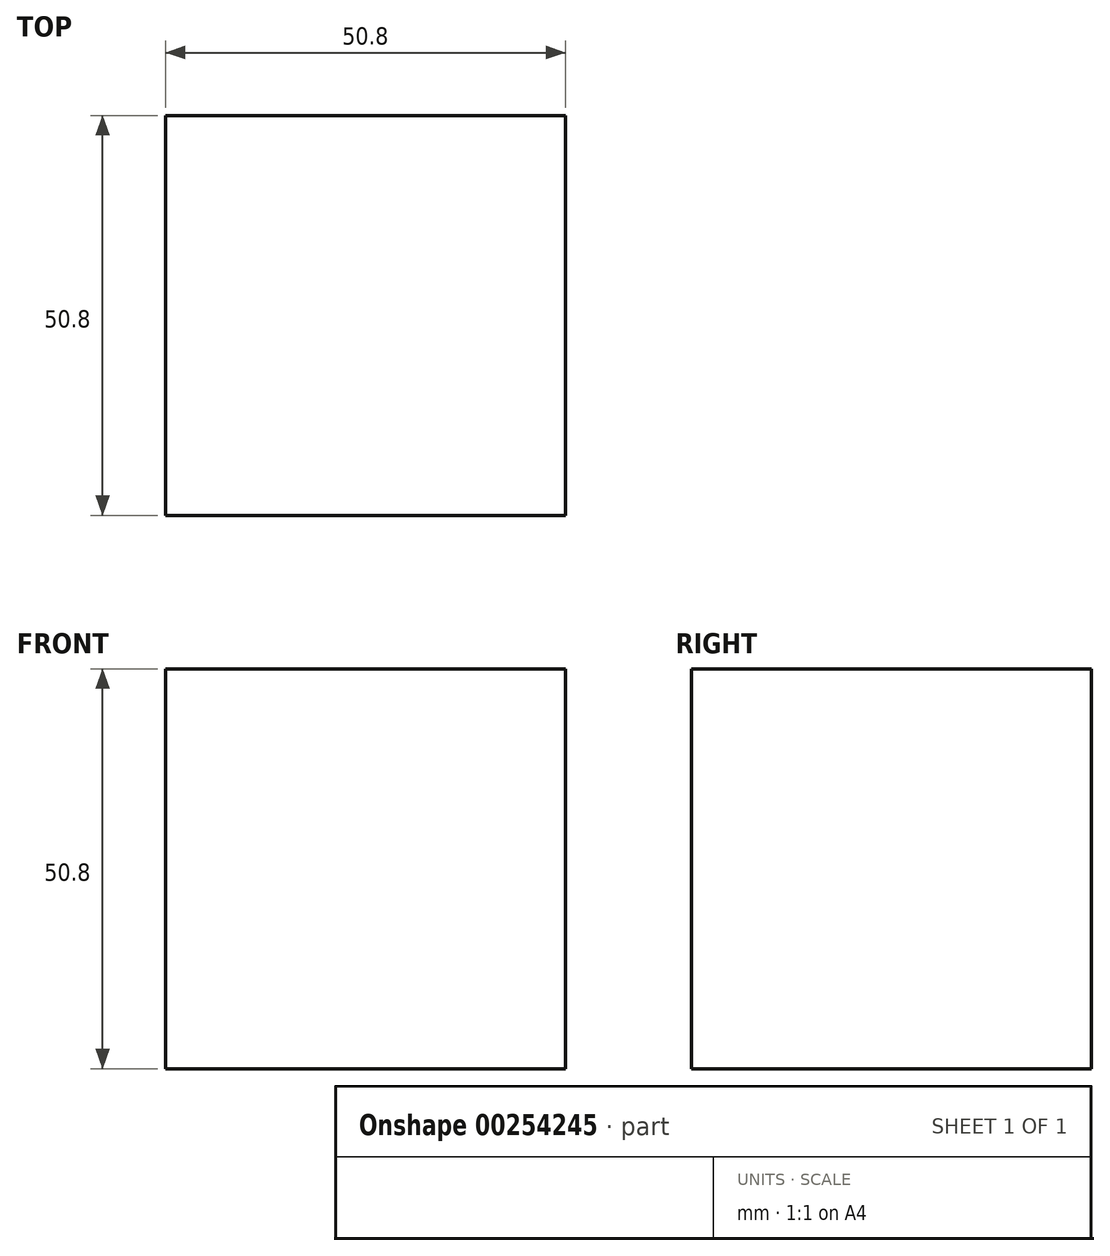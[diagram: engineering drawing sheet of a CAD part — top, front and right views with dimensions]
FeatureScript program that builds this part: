
annotation { "Feature Type Name" : "Feature", "Feature Type Description" : "" }
export const myFeature = defineFeature(function(context is Context, id is Id, definition is map)
    precondition{}
    {
        {
            var Q0;
            Q0=qCreatedBy(makeId("Front.planeOp"),FACE);
            var sketch = newSketch(context, id + "F0", { "sketchPlane" : qUnion([Q0])});
            skLineSegment(sketch, "E0.bottom", {"start": v(20.54, 25.4) * mm, "end": v(-30.26, 25.4) * mm});
            skLineSegment(sketch, "E0.top", {"start": v(20.54, -25.4) * mm, "end": v(-30.26, -25.4) * mm});
            skLineSegment(sketch, "E0.left", {"start": v(20.54, 25.4) * mm, "end": v(20.54, -25.4) * mm});
            skLineSegment(sketch, "E0.right", {"start": v(-30.26, 25.4) * mm, "end": v(-30.26, -25.4) * mm});
            skPoint(sketch, "E0.middle", {"position": v(-4.86, 0) * mm});
            skSolve(sketch);
        }
        {
            var Q0;
            Q0 = qSketchRegion(id + "F0", true);
            extrude(context, id + "F1", {"entities" : qUnion([Q0]), "endBound" : BoundingType.SYMMETRIC, "depth" : 50.8 * mm});
        }
    });
